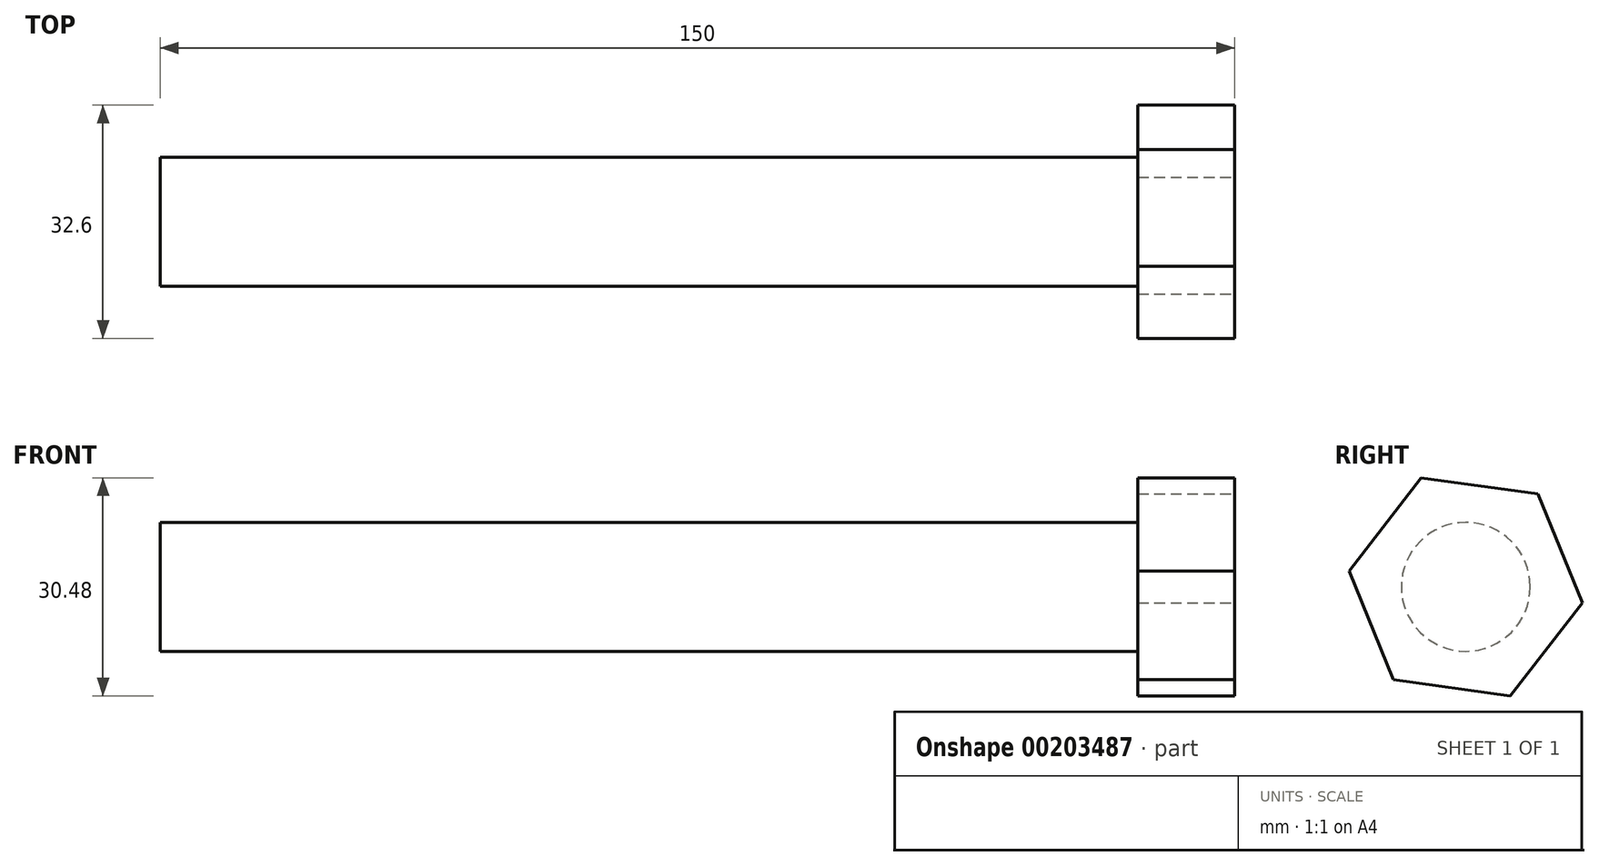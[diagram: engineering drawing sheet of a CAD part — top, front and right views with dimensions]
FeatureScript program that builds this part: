
annotation { "Feature Type Name" : "Feature", "Feature Type Description" : "" }
export const myFeature = defineFeature(function(context is Context, id is Id, definition is map)
    precondition{}
    {
        {
            var Q0;
            Q0=qCreatedBy(makeId("Right.planeOp"),FACE);
            var sketch = newSketch(context, id + "F0", { "sketchPlane" : qUnion([Q0])});
            skCircle(sketch, "E0", {"center": v(0, 0) * mm, "radius": 9 * mm});
            skSolve(sketch);
        }
        {
            var Q0;
            Q0 = qSketchRegion(id + "F0", true);
            extrude(context, id + "F1", {"entities" : qUnion([Q0]), "depth" : 150 * mm});
        }
        {
            var Q0;
            Q0=makeQuery(id+"F1.opExtrude","CAP_FACE",FACE,{"disambiguationData":[OSD([sQuery(id+"F0.wireOp",EDGE,"E0")])],"isStart":false});
            var sketch = newSketch(context, id + "F2", { "sketchPlane" : qUnion([Q0])});
            skCircle(sketch, "E1.cCircle", {"center": v(0, 0) * mm, "radius": 14.25 * mm, "construction": true});
            skLineSegment(sketch, "E1.0", {"start": v(-10.09, -13) * mm, "end": v(-16.3, 2.24) * mm});
            skLineSegment(sketch, "E1.1", {"start": v(-16.3, 2.24) * mm, "end": v(-6.21, 15.24) * mm});
            skLineSegment(sketch, "E1.2", {"start": v(-6.21, 15.24) * mm, "end": v(10.09, 13) * mm});
            skLineSegment(sketch, "E1.3", {"start": v(10.09, 13) * mm, "end": v(16.3, -2.24) * mm});
            skLineSegment(sketch, "E1.4", {"start": v(16.3, -2.24) * mm, "end": v(6.21, -15.24) * mm});
            skLineSegment(sketch, "E1.5", {"start": v(6.21, -15.24) * mm, "end": v(-10.09, -13) * mm});
            skPoint(sketch, "E1.0.midPoint", {"position": v(-13.2, -5.38) * mm});
            skSolve(sketch);
        }
        {
            var Q0;
            Q0 = qSketchRegion(id + "F2", true);
            extrude(context, id + "F3", {"entities" : qUnion([Q0]), "operationType" : NewBodyOperationType.ADD, "oppositeDirection" : true, "depth" : 13.5 * mm});
        }
    });
